# Revit family: Haworth_Janus_Quinta_Table_Occasional
name_source: partatom
category: Furniture
revit_build: Autodesk Revit 2018 (Build: 20170223_1515(x64)
units: mm (PartAtom-declared; Revit-internal decimal feet)

## family parameters
Always vertical = Yes
Cut with Voids When Loaded = No
OmniClass Number = 23.40.70.14.64.21
OmniClass Title = Systems Furniture
Room Calculation Point = No
Shared = No
Work Plane-Based = No

## types (3) — shared parameters
Assembly Code = E2020200
Glide Finish = Haworth _ Polymer _ Black
Manufacturer = Haworth
Revision Number = 2
Size = Verify Final Dim. w/ Haworth
URL = http://www.haworth.com
URL - Product = https://www.haworth.com
Warranty = https://www.haworth.com

## per-type parameters (varying)
| type | Actual Depth | Actual Height | Actual Width | Description | Large Rectangle | Leg Height | Model | Small Rectangle | Square |
| HCJC-QN-TOQ18-J - Square | 17 3/4" | 14" | 17 3/4" | Haworth Janus Quinta - Square Occasional Table | No | 12 37/256" | HCJC-QN-TOQ18-J | No | Yes |
| HCJC-QN-TOR24-J - Small Rectangle | 19" | 16 1/2" | 23 1/2" | Haworth Janus Quinta - Small Rectangle Occasional Table | No | 14 163/256" | HCJC-QN-TOR24-J | Yes | No |
| HCJC-QN-TOR28-J - Large Rectangle | 19 3/4" | 15 3/4" | 27 1/2" | Haworth Janus Quinta - Large Rectangle Occasional Table | Yes | 13 227/256" | HCJC-QN-TOR28-J | No | No |

## geometry (parser evidence)
native form markers: Sweep x2
no freeform markers — native parametric forms only
